# Revit family: Toilet-Floor_Mount-KOHLER-Modflex-K-25042
name_source: partatom
category: Plumbing Fixtures
revit_build: Autodesk Revit 2015 (Build: 20140606_1530(x64)
units: mm (PartAtom-declared; Revit-internal decimal feet)

## types (6) — shared parameters
ADA Compliant = Yes
Assembly Code = D2010100
CW Connection = Yes
Cold Water Inlet = Cold Water Inlet
Date Modified = 03/11/2019
Default Elevation = 0"
Flow Rate = 25 GPM
Flush Rate = 1.6 gpf
HW Connection = No
Height = 17 3/8"
Hot Water Inlet = Hot Water Inlet
Length = 26 3/4"
Manufacturer = KOHLER Co.
MasterFormat 1995 = 15410
MasterFormat 2004 = 22.41.13
Material = Vitreous China
Pressure = 80.00 psi
Product Documentation Link = https://www.us.kohler.com
Product Name = Modflex
Product Page URL = http://www.us.kohler.com
Seat Included = No
URL = https://www.us.kohler.com
Vent Connection = No
Waste Connection = Yes
Waste Water Outlet = Waste Water Outlet
WaterSense Certified = Yes
Width = 16 25/32"

## per-type parameters (varying)
| type | Bedpan Lugs | Description | Finish | Model | Type |
| Antimicrobial Finish, 0-White | No | Modflex Adjust-A-Bowl, Top Spud, Antimicrobial Finish | Kohler-Vitreous_China-0-White | K-25042-SS-0 | 1 |
| Antimicrobial Finish, 47-Almond | No | Modflex Adjust-A-Bowl, Top Spud, Antimicrobial Finish | Kohler-Vitreous_China-47-Almond | K-25042-SS-47 | 2 |
| Antimicrobial Finish, 96-Biscuit | No | Modflex Adjust-A-Bowl, Top Spud, Antimicrobial Finish | Kohler-Vitreous_China-96-Biscuit | K-25042-SS-96 | 3 |
| Antimicrobial Finish, Bedpan Lugs, 0-White | Yes | Modflex Adjust-A-Bowl, Top Spud, Antimicrobial Finish, and Bedpan Lugs | Kohler-Vitreous_China-0-White | K-25042-SSL-0 | 4 |
| Antimicrobial Finish, Bedpan Lugs, 96-Biscuit | Yes | Modflex Adjust-A-Bowl, Top Spud, Antimicrobial Finish, and Bedpan Lugs | Kohler-Vitreous_China-96-Biscuit | K-25042-SSL-96 | 6 |
| Antimicrobial Finish, Bedpan Lugs, 47-Almond | Yes | Modflex Adjust-A-Bowl, Top Spud, Antimicrobial Finish, and Bedpan Lugs | Kohler-Vitreous_China-47-Almond | K-25042-SSL-47 | 5 |

## geometry (parser evidence)
native form markers: Blend x9, Sweep x6
no freeform markers — native parametric forms only
